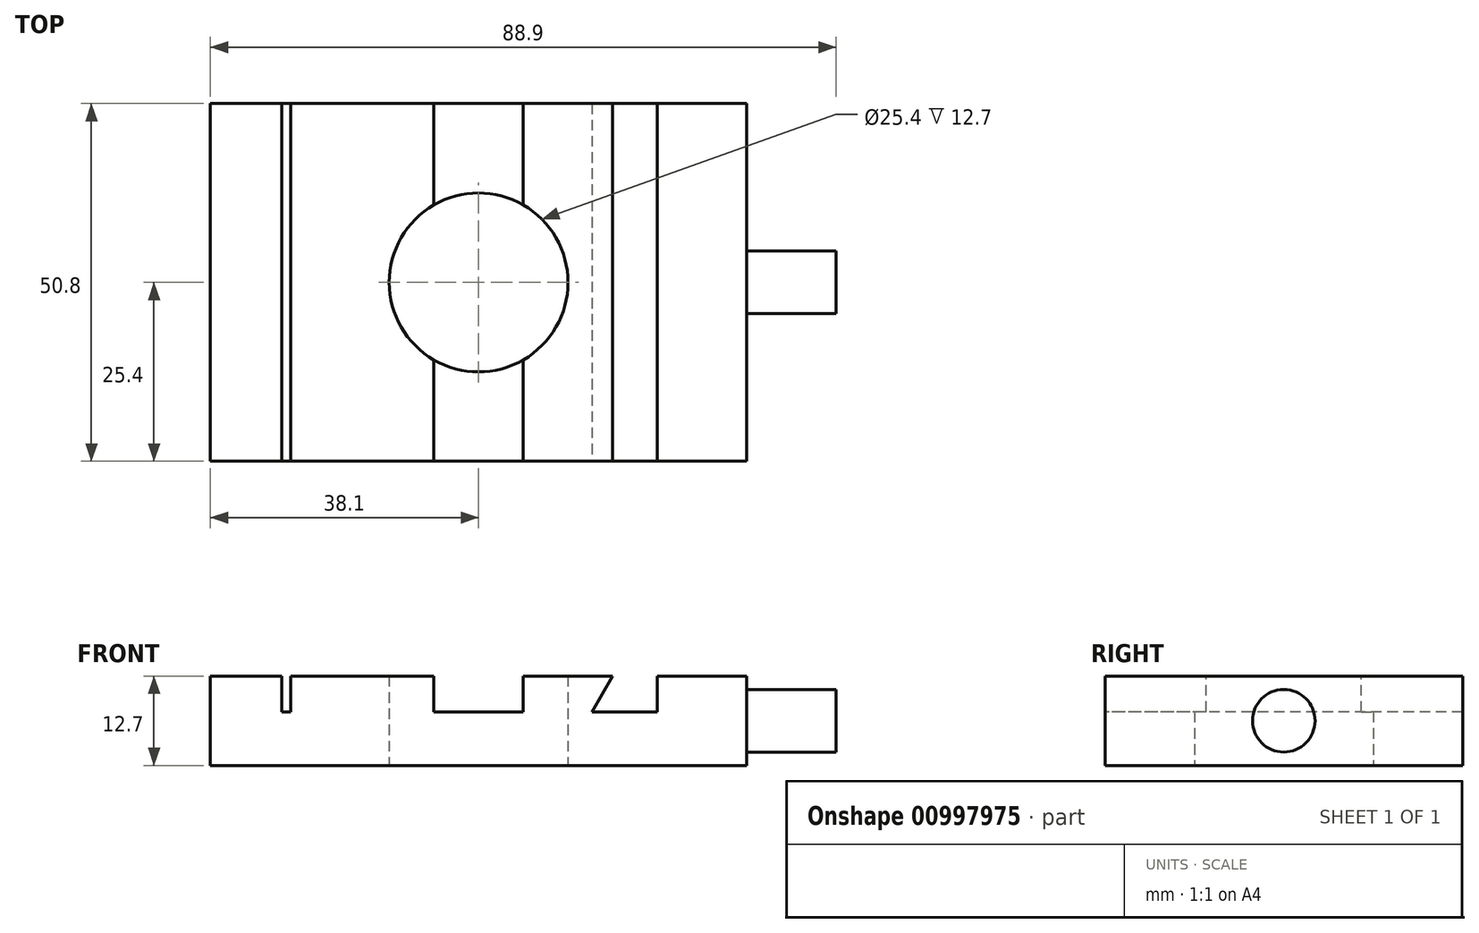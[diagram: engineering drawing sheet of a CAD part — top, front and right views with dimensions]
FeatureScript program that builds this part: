
annotation { "Feature Type Name" : "Feature", "Feature Type Description" : "" }
export const myFeature = defineFeature(function(context is Context, id is Id, definition is map)
    precondition{}
    {
        {
            var Q0;
            Q0=qCreatedBy(makeId("Top.planeOp"),FACE);
            var sketch = newSketch(context, id + "F0", { "sketchPlane" : qUnion([Q0])});
            skLineSegment(sketch, "E0.bottom", {"start": v(-38.1, 25.4) * mm, "end": v(38.1, 25.4) * mm});
            skLineSegment(sketch, "E0.top", {"start": v(-38.1, -25.4) * mm, "end": v(38.1, -25.4) * mm});
            skLineSegment(sketch, "E0.left", {"start": v(-38.1, 25.4) * mm, "end": v(-38.1, -25.4) * mm});
            skLineSegment(sketch, "E0.right", {"start": v(38.1, 25.4) * mm, "end": v(38.1, -25.4) * mm});
            skPoint(sketch, "E0.middle", {"position": v(0, 0) * mm});
            skCircle(sketch, "E1", {"center": v(0, 0) * mm, "radius": 12.7 * mm});
            skSolve(sketch);
        }
        {
            var Q0;
            Q0=makeQuery(id+"F0.imprint","IMPRINT",FACE,{"disambiguationData":[TD([[makeQuery(id+"F0.imprint","IMPRINT",EDGE,{"derivedFrom":sQuery(id+"F0.wireOp",EDGE,"E0.bottom")}),-1.0]])]});
            extrude(context, id + "F1", {"entities" : qUnion([Q0]), "depth" : 12.7 * mm, "offsetDistance" : 25.4 * mm});
        }
        {
            var Q0;
            Q0=makeQuery(id+"F1.opExtrude","CAP_FACE",FACE,{"disambiguationData":[OSD([sQuery(id+"F0.wireOp",EDGE,"E0.bottom"),sQuery(id+"F0.wireOp",EDGE,"E0.top"),sQuery(id+"F0.wireOp",EDGE,"E0.left"),sQuery(id+"F0.wireOp",EDGE,"E0.right"),sQuery(id+"F0.wireOp",EDGE,"E1")])],"isStart":false});
            var sketch = newSketch(context, id + "F2", { "sketchPlane" : qUnion([Q0])});
            skLineSegment(sketch, "E2.bottom", {"start": v(-27.94, 25.4) * mm, "end": v(-26.67, 25.4) * mm});
            skLineSegment(sketch, "E2.top", {"start": v(-27.94, -25.4) * mm, "end": v(-26.67, -25.4) * mm});
            skLineSegment(sketch, "E2.left", {"start": v(-27.94, 25.4) * mm, "end": v(-27.94, -25.4) * mm});
            skLineSegment(sketch, "E2.right", {"start": v(-26.67, 25.4) * mm, "end": v(-26.67, -25.4) * mm});
            skLineSegment(sketch, "E3", {"start": v(-6.35, 25.4) * mm, "end": v(-6.35, -25.4) * mm});
            skLineSegment(sketch, "E4", {"start": v(-6.35, -25.4) * mm, "end": v(6.35, -25.4) * mm});
            skLineSegment(sketch, "E5", {"start": v(6.35, -25.4) * mm, "end": v(6.35, 25.4) * mm});
            skLineSegment(sketch, "E6", {"start": v(-6.35, 25.4) * mm, "end": v(6.35, 25.4) * mm});
            skPoint(sketch, "E7", {"position": v(0, 0) * mm});
            skLineSegment(sketch, "E8", {"start": v(0, 25.4) * mm, "end": v(0, -25.4) * mm, "construction": true});
            skSolve(sketch);
        }
        {
            var Q0;
            Q0=makeQuery(id+"F2.imprint","IMPRINT",FACE,{"disambiguationData":[TD([[makeQuery(id+"F2.imprint","IMPRINT",EDGE,{"derivedFrom":sQuery(id+"F2.wireOp",EDGE,"E2.bottom")}),-1.0]])]});
            var Q1;
            {var subQ0=sQuery(id+"F2.wireOp",EDGE,"E6");Q1=makeQuery(id+"F2.imprint","IMPRINT",FACE,{"disambiguationData":[TD([[makeQuery(id+"F2.imprint","IMPRINT",EDGE,{"derivedFrom":subQ0}),-1.0]])]});}
            var Q2;
            {var subQ0=sQuery(id+"F2.wireOp",EDGE,"E4");Q2=makeQuery(id+"F2.imprint","IMPRINT",FACE,{"disambiguationData":[TD([[makeQuery(id+"F2.imprint","IMPRINT",EDGE,{"derivedFrom":subQ0}),1.0]])]});}
            extrude(context, id + "F3", {"entities" : qUnion([Q0, Q1, Q2]), "operationType" : NewBodyOperationType.REMOVE, "oppositeDirection" : true, "depth" : 5.08 * mm, "offsetDistance" : 25.4 * mm});
        }
        {
            var Q0;
            Q0=makeQuery(id+"F1.opExtrude","SWEPT_FACE",FACE,{"disambiguationData":[OSD([sQuery(id+"F0.wireOp",EDGE,"E0.top")])]});
            var sketch = newSketch(context, id + "F4", { "sketchPlane" : qUnion([Q0])});
            skLineSegment(sketch, "E9", {"start": v(19.05, 12.7) * mm, "end": v(16.12, 7.62) * mm});
            skLineSegment(sketch, "E10", {"start": v(34.68, 7.62) * mm, "end": v(31.75, 12.7) * mm});
            skLineSegment(sketch, "E11", {"start": v(31.75, 12.7) * mm, "end": v(34.68, 7.62) * mm});
            skLineSegment(sketch, "E12", {"start": v(16.12, 7.62) * mm, "end": v(34.68, 7.62) * mm});
            skLineSegment(sketch, "E13", {"start": v(31.75, 12.7) * mm, "end": v(19.05, 12.7) * mm});
            skLineSegment(sketch, "E14", {"start": v(25.4, 7.62) * mm, "end": v(25.4, 12.7) * mm});
            skSolve(sketch);
        }
        {
            var Q0;
            {var subQ0=sQuery(id+"F4.wireOp",EDGE,"E9");Q0=makeQuery(id+"F4.imprint","IMPRINT",FACE,{"disambiguationData":[TD([[makeQuery(id+"F4.imprint","IMPRINT",EDGE,{"derivedFrom":subQ0}),1.0]])]});}
            var Q1;
            {var subQ0=sQuery(id+"F4.wireOp",EDGE,"E11");Q1=makeQuery(id+"F4.imprint","IMPRINT",FACE,{"disambiguationData":[TD([[makeQuery(id+"F4.imprint","IMPRINT",EDGE,{"derivedFrom":subQ0}),-1.0]])]});}
            extrude(context, id + "F5", {"entities" : qUnion([Q0, Q1]), "operationType" : NewBodyOperationType.REMOVE, "endBound" : BoundingType.THROUGH_ALL, "oppositeDirection" : true, "depth" : 25.4 * mm, "offsetDistance" : 25.4 * mm});
        }
        {
            var Q0;
            Q0=makeQuery(id+"F1.opExtrude","SWEPT_FACE",FACE,{"disambiguationData":[OSD([sQuery(id+"F0.wireOp",EDGE,"E0.right")])]});
            var sketch = newSketch(context, id + "F6", { "sketchPlane" : qUnion([Q0])});
            skCircle(sketch, "E15", {"center": v(0, 6.35) * mm, "radius": 4.45 * mm});
            skPoint(sketch, "E15.centerSnap0", {"position": v(-25.4, 6.35) * mm});
            skPoint(sketch, "E15.centerSnap1", {"position": v(0, 12.7) * mm});
            skSolve(sketch);
        }
        {
            var Q0;
            Q0=makeQuery(id+"F6.imprint","IMPRINT",FACE,{"disambiguationData":[TD([[makeQuery(id+"F6.imprint","IMPRINT",EDGE,{"derivedFrom":sQuery(id+"F6.wireOp",EDGE,"E15")}),1.0]])]});
            var Q1;
            Q1=sQuery(id+"F6.wireOp",EDGE,"E15");
            extrude(context, id + "F7", {"entities" : qUnion([Q0]), "operationType" : NewBodyOperationType.ADD, "surfaceEntities" : qUnion([Q1]), "depth" : 12.7 * mm, "offsetDistance" : 25.4 * mm});
        }
    });
